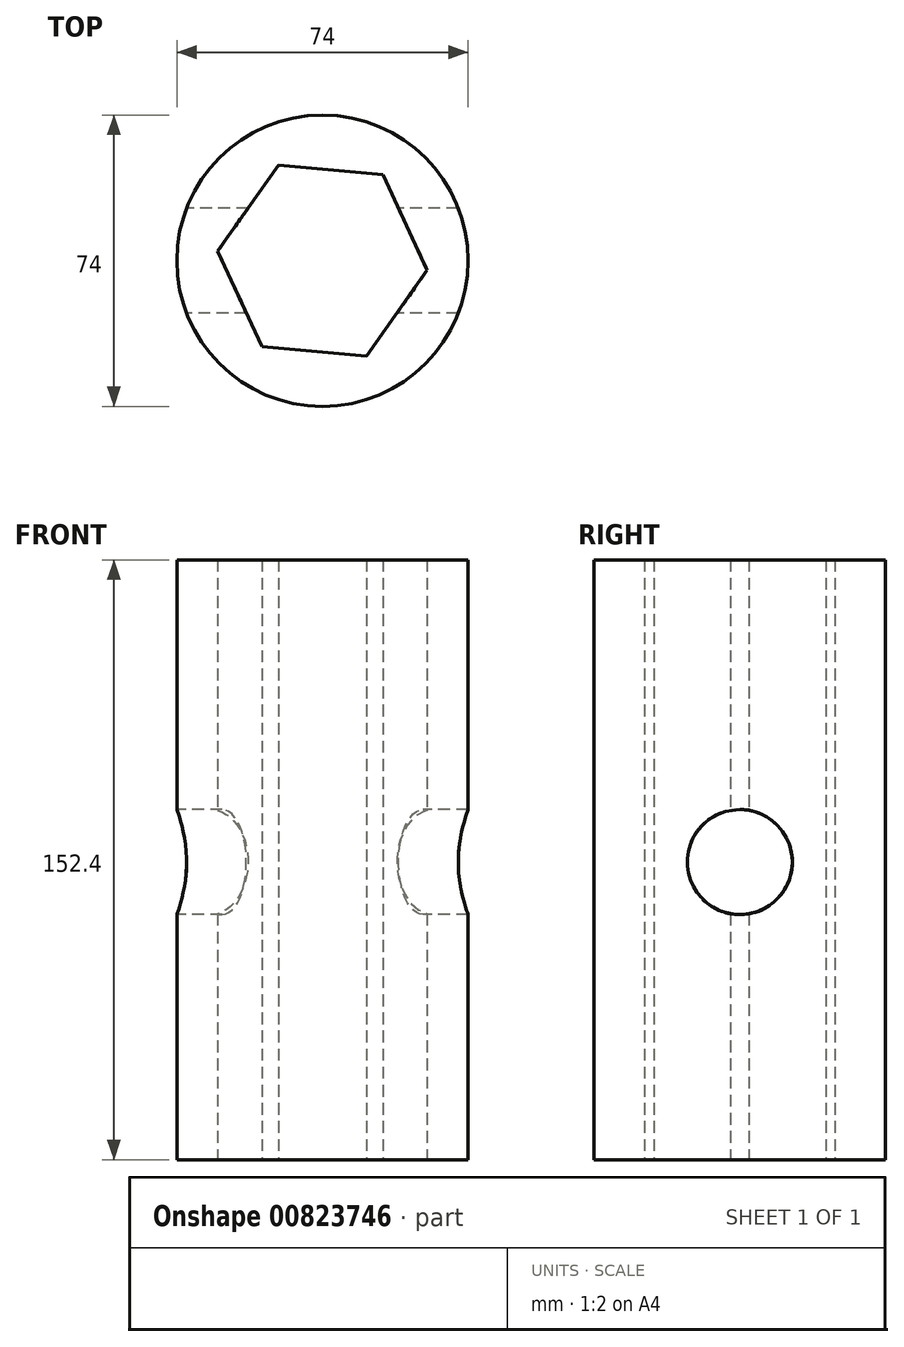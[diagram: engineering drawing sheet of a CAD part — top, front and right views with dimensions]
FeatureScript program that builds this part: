
annotation { "Feature Type Name" : "Feature", "Feature Type Description" : "" }
export const myFeature = defineFeature(function(context is Context, id is Id, definition is map)
    precondition{}
    {
        {
            var Q0;
            Q0=qCreatedBy(makeId("Top.planeOp"),FACE);
            var sketch = newSketch(context, id + "F0", { "sketchPlane" : qUnion([Q0])});
            skCircle(sketch, "E0.cCircle", {"center": v(0, 0) * mm, "radius": 23.14 * mm, "construction": true});
            skLineSegment(sketch, "E0.0", {"start": v(-15.39, -21.84) * mm, "end": v(-26.6, 2.4) * mm});
            skLineSegment(sketch, "E0.1", {"start": v(-26.6, 2.4) * mm, "end": v(-11.22, 24.25) * mm});
            skLineSegment(sketch, "E0.2", {"start": v(-11.22, 24.25) * mm, "end": v(15.39, 21.84) * mm});
            skLineSegment(sketch, "E0.3", {"start": v(15.39, 21.84) * mm, "end": v(26.6, -2.4) * mm});
            skLineSegment(sketch, "E0.4", {"start": v(26.6, -2.4) * mm, "end": v(11.22, -24.25) * mm});
            skLineSegment(sketch, "E0.5", {"start": v(11.22, -24.25) * mm, "end": v(-15.39, -21.84) * mm});
            skPoint(sketch, "E0.0.midPoint", {"position": v(-21, -9.72) * mm});
            skCircle(sketch, "E1", {"center": v(0, 0) * mm, "radius": 37 * mm});
            skSolve(sketch);
        }
        {
            var Q0;
            Q0=makeQuery(id+"F0.imprint","IMPRINT",FACE,{"disambiguationData":[TD([[makeQuery(id+"F0.imprint","IMPRINT",EDGE,{"derivedFrom":sQuery(id+"F0.wireOp",EDGE,"E0.0")}),1.0]])]});
            extrude(context, id + "F1", {"entities" : qUnion([Q0]), "depth" : 152.4 * mm, "offsetDistance" : 25.4 * mm});
        }
        {
            var Q0;
            Q0=qCreatedBy(makeId("Right.planeOp"),FACE);
            var sketch = newSketch(context, id + "F2", { "sketchPlane" : qUnion([Q0])});
            skCircle(sketch, "E2", {"center": v(0, 75.63) * mm, "radius": 13.36 * mm});
            skSolve(sketch);
        }
        {
            var Q0;
            Q0 = qSketchRegion(id + "F2", true);
            extrude(context, id + "F3", {"entities" : qUnion([Q0]), "operationType" : NewBodyOperationType.REMOVE, "depth" : 228.6 * mm, "offsetDistance" : 25.4 * mm, "hasSecondDirection" : true, "secondDirectionOppositeDirection" : true, "secondDirectionDepth" : 228.6 * mm});
        }
    });
